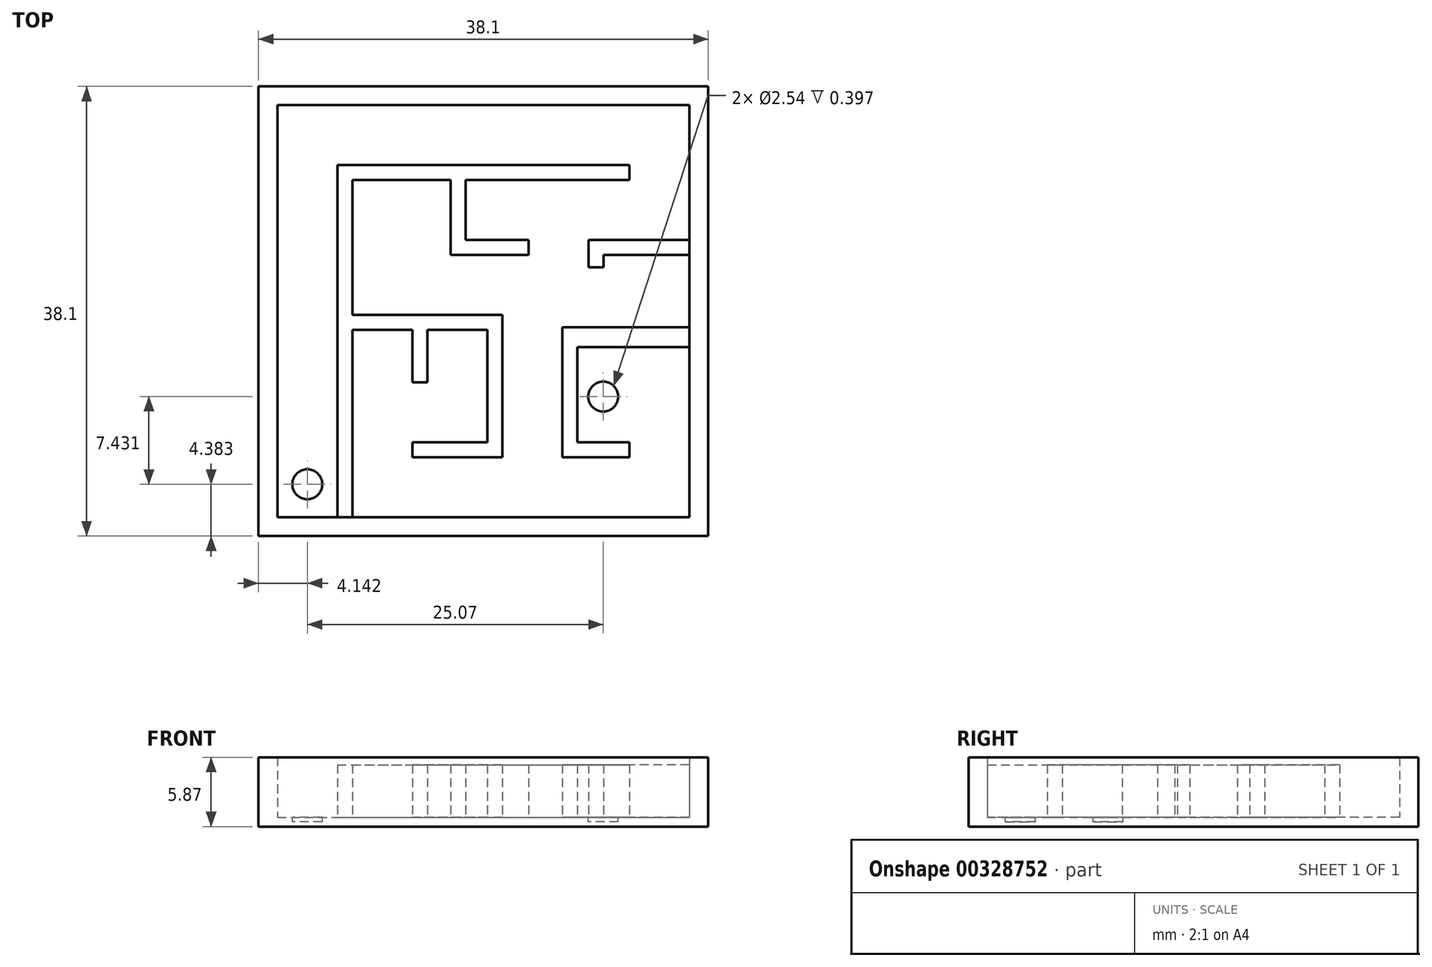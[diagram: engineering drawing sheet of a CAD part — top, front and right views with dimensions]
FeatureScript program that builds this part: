
annotation { "Feature Type Name" : "Feature", "Feature Type Description" : "" }
export const myFeature = defineFeature(function(context is Context, id is Id, definition is map)
    precondition{}
    {
        {
            var Q0;
            Q0=qCreatedBy(makeId("Top.planeOp"),FACE);
            var sketch = newSketch(context, id + "F0", { "sketchPlane" : qUnion([Q0])});
            skLineSegment(sketch, "E0.bottom", {"start": v(-22, 19.7) * mm, "end": v(16.1, 19.7) * mm});
            skLineSegment(sketch, "E0.top", {"start": v(-22, -18.4) * mm, "end": v(16.1, -18.4) * mm});
            skLineSegment(sketch, "E0.left", {"start": v(-22, 19.7) * mm, "end": v(-22, -18.4) * mm});
            skLineSegment(sketch, "E0.right", {"start": v(16.1, 19.7) * mm, "end": v(16.1, -18.4) * mm});
            skSolve(sketch);
        }
        {
            var Q0;
            Q0=makeQuery(id+"F0.imprint","IMPRINT",FACE,{"disambiguationData":[TD([[makeQuery(id+"F0.imprint","IMPRINT",EDGE,{"derivedFrom":sQuery(id+"F0.wireOp",EDGE,"E0.bottom")}),-1.0]])]});
            extrude(context, id + "F1", {"entities" : qUnion([Q0]), "depth" : 0.8 * mm});
        }
        {
            var Q0;
            Q0=makeQuery(id+"F1.opExtrude","CAP_FACE",FACE,{"disambiguationData":[OSD([sQuery(id+"F0.wireOp",EDGE,"E0.bottom"),sQuery(id+"F0.wireOp",EDGE,"E0.top"),sQuery(id+"F0.wireOp",EDGE,"E0.left"),sQuery(id+"F0.wireOp",EDGE,"E0.right")])],"isStart":false});
            var sketch = newSketch(context, id + "F2", { "sketchPlane" : qUnion([Q0])});
            skLineSegment(sketch, "E1.0", {"start": v(-20.4, 18.1) * mm, "end": v(14.5, 18.1) * mm});
            skLineSegment(sketch, "E1.1", {"start": v(-20.4, 18.1) * mm, "end": v(-20.4, -16.8) * mm});
            skLineSegment(sketch, "E1.2", {"start": v(-20.4, -16.8) * mm, "end": v(14.5, -16.8) * mm});
            skLineSegment(sketch, "E1.3", {"start": v(14.5, 18.1) * mm, "end": v(14.5, -16.8) * mm});
            skSolve(sketch);
        }
        {
            var Q0;
            Q0=makeQuery(id+"F2.imprint","IMPRINT",FACE,{"disambiguationData":[TD([[makeQuery(id+"F2.imprint","IMPRINT",EDGE,{"derivedFrom":sQuery(id+"F2.wireOp",EDGE,"E1.0")}),1.0]])]});
            extrude(context, id + "F3", {"entities" : qUnion([Q0]), "operationType" : NewBodyOperationType.ADD, "depth" : 5.08 * mm});
        }
        {
            var Q0;
            Q0=makeQuery(id+"F1.opExtrude","CAP_FACE",FACE,{"disambiguationData":[OSD([sQuery(id+"F0.wireOp",EDGE,"E0.bottom"),sQuery(id+"F0.wireOp",EDGE,"E0.top"),sQuery(id+"F0.wireOp",EDGE,"E0.left"),sQuery(id+"F0.wireOp",EDGE,"E0.right")])],"isStart":false});
            var sketch = newSketch(context, id + "F4", { "sketchPlane" : qUnion([Q0])});
            skLineSegment(sketch, "E2.bottom", {"start": v(-15.32, -16.8) * mm, "end": v(-14.05, -16.8) * mm});
            skLineSegment(sketch, "E2.top", {"start": v(-15.32, 13.01) * mm, "end": v(-14.05, 13.01) * mm});
            skLineSegment(sketch, "E2.left", {"start": v(-15.32, -16.8) * mm, "end": v(-15.32, 13.01) * mm});
            skLineSegment(sketch, "E2.right", {"start": v(-14.05, -16.8) * mm, "end": v(-14.05, -0.96) * mm});
            skLineSegment(sketch, "E3.bottom", {"start": v(-14.05, 13.01) * mm, "end": v(9.42, 13.01) * mm});
            skLineSegment(sketch, "E3.top", {"start": v(-14.05, 11.74) * mm, "end": v(-5.72, 11.74) * mm});
            skLineSegment(sketch, "E3.right", {"start": v(9.42, 13.01) * mm, "end": v(9.42, 11.74) * mm});
            skLineSegment(sketch, "E4.bottom", {"start": v(14.5, 6.66) * mm, "end": v(5.97, 6.66) * mm});
            skLineSegment(sketch, "E4.top", {"start": v(14.5, 5.4) * mm, "end": v(7.24, 5.4) * mm});
            skLineSegment(sketch, "E4.left", {"start": v(14.5, 6.66) * mm, "end": v(14.5, 5.4) * mm});
            skLineSegment(sketch, "E4.right", {"start": v(5.97, 6.66) * mm, "end": v(5.97, 5.4) * mm});
            skLineSegment(sketch, "E5.bottom", {"start": v(5.97, 6.66) * mm, "end": v(7.08, 6.66) * mm});
            skLineSegment(sketch, "E6.right", {"start": v(12.66, -0.96) * mm, "end": v(12.66, 0.31) * mm});
            skLineSegment(sketch, "E7.top", {"start": v(-5.72, 5.4) * mm, "end": v(-4.45, 5.4) * mm});
            skLineSegment(sketch, "E7.left", {"start": v(-5.72, 11.74) * mm, "end": v(-5.72, 5.4) * mm});
            skLineSegment(sketch, "E7.right", {"start": v(-4.45, 11.74) * mm, "end": v(-4.45, 6.66) * mm});
            skLineSegment(sketch, "E8.bottom", {"start": v(-5.72, 5.4) * mm, "end": v(0.9, 5.4) * mm});
            skLineSegment(sketch, "E8.top", {"start": v(-4.45, 6.66) * mm, "end": v(0.9, 6.66) * mm});
            skLineSegment(sketch, "E8.left", {"start": v(-5.72, 5.4) * mm, "end": v(-5.72, 6.66) * mm});
            skLineSegment(sketch, "E8.right", {"start": v(0.9, 5.4) * mm, "end": v(0.9, 6.66) * mm});
            skLineSegment(sketch, "E9.bottom", {"start": v(-14.05, 0.31) * mm, "end": v(-1.35, 0.31) * mm});
            skLineSegment(sketch, "E9.top", {"start": v(-14.05, -0.96) * mm, "end": v(-8.97, -0.96) * mm});
            skLineSegment(sketch, "E9.right", {"start": v(-1.35, 0.31) * mm, "end": v(-1.35, -0.96) * mm});
            skLineSegment(sketch, "E10.top", {"start": v(-1.35, -11.73) * mm, "end": v(-2.62, -11.73) * mm});
            skLineSegment(sketch, "E10.left", {"start": v(-1.35, -0.96) * mm, "end": v(-1.35, -11.73) * mm});
            skLineSegment(sketch, "E10.right", {"start": v(-2.62, -0.96) * mm, "end": v(-2.62, -10.46) * mm});
            skLineSegment(sketch, "E11.bottom", {"start": v(-2.62, -11.73) * mm, "end": v(-8.97, -11.73) * mm});
            skLineSegment(sketch, "E11.top", {"start": v(-2.62, -10.46) * mm, "end": v(-8.97, -10.46) * mm});
            skLineSegment(sketch, "E11.right", {"start": v(-8.97, -11.73) * mm, "end": v(-8.97, -10.46) * mm});
            skPoint(sketch, "E12.oppositeSnap0", {"position": v(-7.7, -0.96) * mm});
            skLineSegment(sketch, "E12.top", {"start": v(-8.97, -5.38) * mm, "end": v(-7.7, -5.38) * mm});
            skLineSegment(sketch, "E12.left", {"start": v(-8.97, -0.96) * mm, "end": v(-8.97, -5.38) * mm});
            skLineSegment(sketch, "E12.right", {"start": v(-7.7, -0.96) * mm, "end": v(-7.7, -5.38) * mm});
            skLineSegment(sketch, "E13.bottom", {"start": v(14.5, -0.72) * mm, "end": v(3.73, -0.72) * mm});
            skLineSegment(sketch, "E13.top", {"start": v(14.5, -2.41) * mm, "end": v(5, -2.41) * mm});
            skLineSegment(sketch, "E13.left", {"start": v(14.5, -0.72) * mm, "end": v(14.5, -2.41) * mm});
            skLineSegment(sketch, "E13.right", {"start": v(3.73, -0.72) * mm, "end": v(3.73, -2.41) * mm});
            skLineSegment(sketch, "E14.bottom", {"start": v(3.73, -0.72) * mm, "end": v(5, -0.72) * mm});
            skLineSegment(sketch, "E14.left", {"start": v(3.73, -0.72) * mm, "end": v(3.73, -10.46) * mm});
            skLineSegment(sketch, "E14.right", {"start": v(5, -2.41) * mm, "end": v(5, -10.46) * mm});
            skLineSegment(sketch, "E15.bottom", {"start": v(5, -11.73) * mm, "end": v(9.42, -11.73) * mm});
            skLineSegment(sketch, "E15.top", {"start": v(5, -10.46) * mm, "end": v(9.42, -10.46) * mm});
            skLineSegment(sketch, "E15.right", {"start": v(9.42, -11.73) * mm, "end": v(9.42, -10.46) * mm});
            skLineSegment(sketch, "E16.trimOffspring", {"start": v(-4.45, 11.74) * mm, "end": v(9.42, 11.74) * mm});
            skLineSegment(sketch, "E17.trimOffspring", {"start": v(-7.7, -0.96) * mm, "end": v(-2.62, -0.96) * mm});
            skLineSegment(sketch, "E18.trimOffspring", {"start": v(-14.05, 0.31) * mm, "end": v(-14.05, 11.74) * mm});
            skLineSegment(sketch, "E19", {"start": v(5, -11.73) * mm, "end": v(3.73, -11.73) * mm});
            skLineSegment(sketch, "E20", {"start": v(3.73, -11.73) * mm, "end": v(3.73, -10.46) * mm});
            skLineSegment(sketch, "E21", {"start": v(5.97, 5.4) * mm, "end": v(5.97, 4.36) * mm});
            skLineSegment(sketch, "E22", {"start": v(5.97, 4.36) * mm, "end": v(7.24, 4.36) * mm});
            skLineSegment(sketch, "E23", {"start": v(7.24, 4.36) * mm, "end": v(7.24, 5.4) * mm});
            skLineSegment(sketch, "E24", {"start": v(-20.4, -16.8) * mm, "end": v(-15.32, -16.8) * mm});
            skCircle(sketch, "E25", {"center": v(-17.86, -14.03) * mm, "radius": 1.27 * mm});
            skPoint(sketch, "E25.centerSnap0", {"position": v(-17.86, -16.8) * mm});
            skCircle(sketch, "E26", {"center": v(7.21, -6.6) * mm, "radius": 1.27 * mm});
            skPoint(sketch, "E26.centerSnap0", {"position": v(7.21, -10.46) * mm});
            skSolve(sketch);
        }
        {
            var Q0;
            Q0=makeQuery(id+"F4.imprint","IMPRINT",FACE,{"disambiguationData":[TD([[makeQuery(id+"F4.imprint","IMPRINT",EDGE,{"derivedFrom":sQuery(id+"F4.wireOp",EDGE,"E25")}),1.0]])]});
            var Q1;
            Q1=makeQuery(id+"F4.imprint","IMPRINT",FACE,{"disambiguationData":[TD([[makeQuery(id+"F4.imprint","IMPRINT",EDGE,{"derivedFrom":sQuery(id+"F4.wireOp",EDGE,"E26")}),1.0]])]});
            extrude(context, id + "F5", {"entities" : qUnion([Q0, Q1]), "operationType" : NewBodyOperationType.REMOVE, "oppositeDirection" : true, "depth" : 0.4 * mm});
        }
        {
            var Q0;
            Q0=makeQuery(id+"F4.imprint","IMPRINT",FACE,{"disambiguationData":[TD([[makeQuery(id+"F4.imprint","IMPRINT",EDGE,{"derivedFrom":sQuery(id+"F4.wireOp",EDGE,"E2.bottom")}),1.0]])]});
            var Q1;
            Q1=makeQuery(id+"F4.imprint","IMPRINT",FACE,{"disambiguationData":[TD([[makeQuery(id+"F4.imprint","IMPRINT",EDGE,{"derivedFrom":sQuery(id+"F4.wireOp",EDGE,"E13.top")}),-1.0]])]});
            var Q2;
            Q2=makeQuery(id+"F4.imprint","IMPRINT",FACE,{"disambiguationData":[TD([[makeQuery(id+"F4.imprint","IMPRINT",EDGE,{"derivedFrom":sQuery(id+"F4.wireOp",EDGE,"E4.bottom")}),1.0]])]});
            extrude(context, id + "F6", {"entities" : qUnion([Q0, Q1, Q2]), "operationType" : NewBodyOperationType.ADD, "depth" : 4.44 * mm});
        }
    });
